# Revit family: BOVER_Pendant_Outdoor_Garota_USA_S-02_Brown_Led
name_source: partatom
category: Lighting Fixtures
revit_build: Autodesk Revit 2017 (Build: 20181011_1645(x64)
units: mm (PartAtom-declared; Revit-internal decimal feet)

## family parameters
Cut with Voids When Loaded = No
Host = Face
Light Source = Yes
OmniClass Number = 23.80.70.11.14
OmniClass Title = General Luminaries, Directional
Part Type = Normal
Room Calculation Point = No
Round Connector Dimension = Use Diameter
Shared = No

## types (1)
- GAROTA_S-02_USA_Brown Shade_Graphite Brown_LED
    Apparent Load = 0 VA
    Assembly Code = 0
    CRI = 90
    Cable.Electric.Material = Bover.Graphite.Brown
    Canopy.Material = Bover.Graphite.Brown
    Color Filter = 16777215
    Default Elevation = 50 "
    Diffuser.Material = Bover.Glass.Borosilicate.Frosted.White
    Dimming = No
    Dimming Lamp Color Temperature Shift = <None>
    Driver Type = CC – Constant Current
    Ean13 = 8435493717135
    Emit Shape Visible in Rendering = No
    Emit from Circle Diameter = 2 "
    Environment = Outdoor
    Frequency = 60Hz
    Gama = Pendant Luminaire
    Ingress Protection = IP66
    Lamp = 2 x 10 W E26 LED A19
    Lamp Type = LED
    Led.Material = Bover.Light.Screen.2700K
    Manufacturer = BOVER
    Number of Poles = 1
    Photometric Web File = GAROTA S 02 33502202xxU+P801 MARRON E26 20W USA.IES
    Power Factor = 0
    Product = Garota S/02
    Product URL = https://www.bover.es
    Reference = 3350220203U/P802
    Revit Model Autor = A3D Consulting
    Revit Model Autor URL = www.a3d.es
    Revit Model Version = 1.0
    Tensor.Material = Bover.Metal.Stainless Steel
    Tilt Angle = 90.00°
    URL = www.bover.es
    Voltage = 120 V
    Voltage Input (min-max) = 120V

## geometry (parser evidence)
native form markers: Sweep x3
no freeform markers — native parametric forms only
